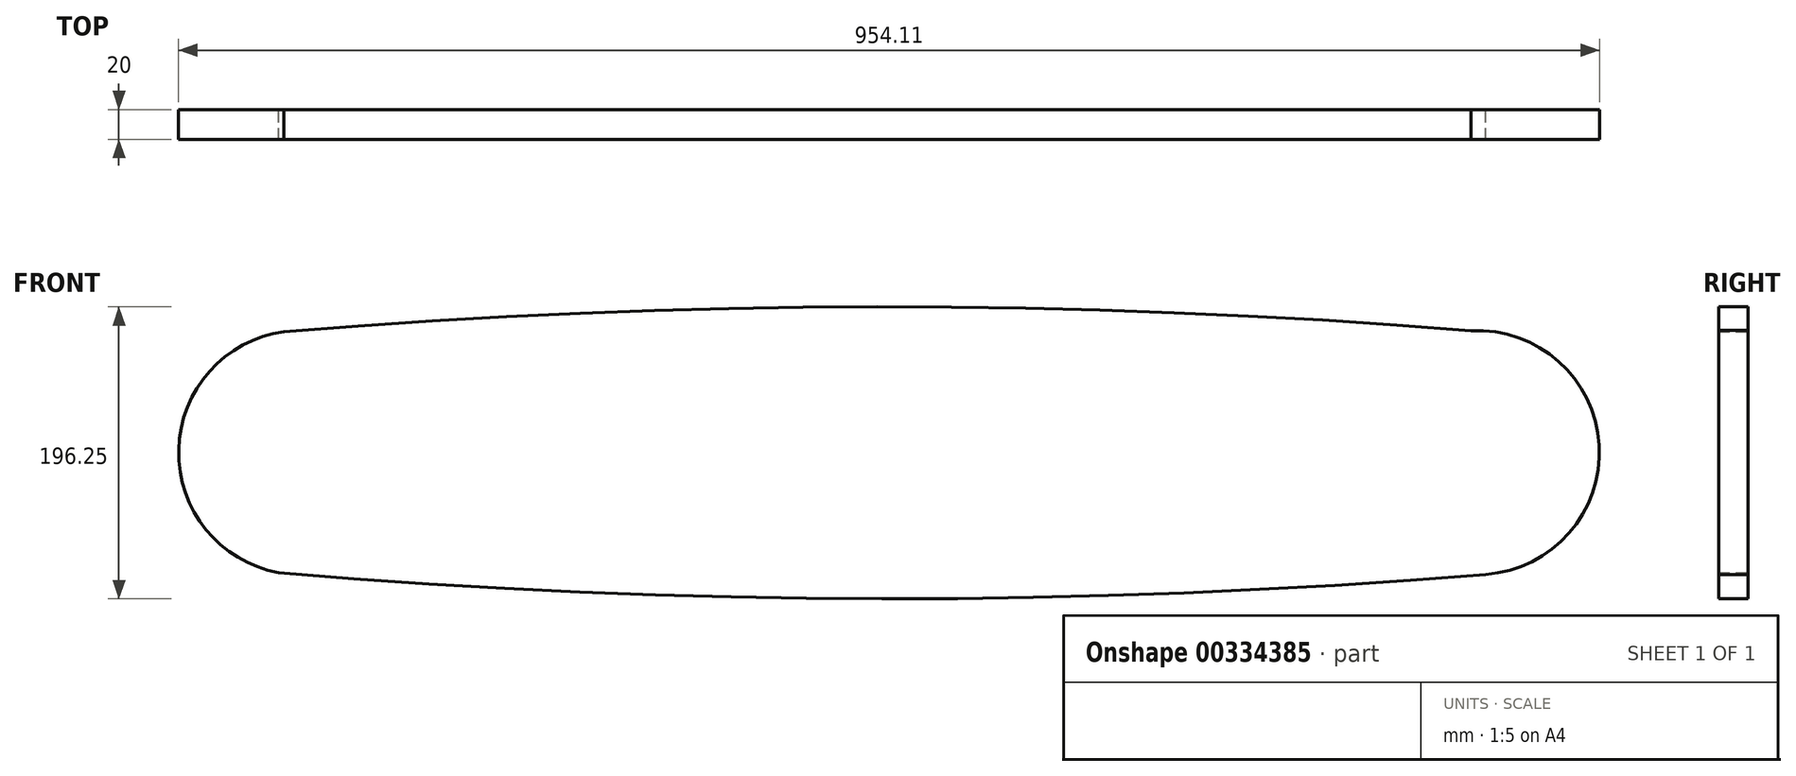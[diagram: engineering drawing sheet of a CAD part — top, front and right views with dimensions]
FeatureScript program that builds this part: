
annotation { "Feature Type Name" : "Feature", "Feature Type Description" : "" }
export const myFeature = defineFeature(function(context is Context, id is Id, definition is map)
    precondition{}
    {
        {
            var Q0;
            Q0=qCreatedBy(makeId("Front.planeOp"),FACE);
            var sketch = newSketch(context, id + "F0", { "sketchPlane" : qUnion([Q0])});
            skCircle(sketch, "E0", {"center": v(-47.6, 0) * mm, "radius": 82.06 * mm});
            skCircle(sketch, "E1", {"center": v(742.4, 0) * mm, "radius": 82.06 * mm});
            skLineSegment(sketch, "E2", {"start": v(-47.6, 0) * mm, "end": v(742.4, 0) * mm});
            skArc(sketch, "E3", {"start": v(-62.59, -80.67) * mm, "mid": v(342.73, -98.23) * mm, "end": v(748.1, -81.86) * mm});
            skArc(sketch, "E4", {"start": v(738.11, 81.94) * mm, "mid": v(339.6, 98) * mm, "end": v(-58.9, 81.27) * mm});
            skSolve(sketch);
        }
        {
            var Q0;
            {var subQ1=sQuery(id+"F0.wireOp",EDGE,"E0");var subQ5=sQuery(id+"F0.wireOp",EDGE,"E4");var subQ7=makeQuery(id+"F0.imprint","INTERSECT",VERTEX,{"disambiguationData":[OD(1.0)],"derivedFrom":[subQ1,subQ5]});Q0=makeQuery(id+"F0.imprint","IMPRINT",FACE,{"disambiguationData":[TD([[makeQuery(id+"F0.imprint","IMPRINT",EDGE,{"disambiguationData":[TD([[subQ7,1.0]])],"derivedFrom":subQ1}),1.0]])]});}
            var Q1;
            {var subQ0=sQuery(id+"F0.wireOp",EDGE,"E4");var subQ1=sQuery(id+"F0.wireOp",EDGE,"E0");var subQ2=makeQuery(id+"F0.imprint","INTERSECT",VERTEX,{"disambiguationData":[OD(1.0)],"derivedFrom":[subQ1,subQ0]});Q1=makeQuery(id+"F0.imprint","IMPRINT",FACE,{"disambiguationData":[TD([[makeQuery(id+"F0.imprint","IMPRINT",EDGE,{"disambiguationData":[TD([[subQ2,1.0]])],"derivedFrom":subQ1}),-1.0]])]});}
            var Q2;
            {var subQ0=sQuery(id+"F0.wireOp",EDGE,"E2");var subQ1=sQuery(id+"F0.wireOp",EDGE,"E0");var subQ2=makeQuery(id+"F0.imprint","INTERSECT",VERTEX,{"derivedFrom":[subQ1,subQ0]});Q2=makeQuery(id+"F0.imprint","IMPRINT",FACE,{"disambiguationData":[TD([[makeQuery(id+"F0.imprint","IMPRINT",EDGE,{"disambiguationData":[TD([[subQ2,1.0]])],"derivedFrom":subQ1}),-1.0]])]});}
            var Q3;
            {var subQ0=sQuery(id+"F0.wireOp",EDGE,"E1");var subQ1=makeQuery(id+"F0.imprint","INTERSECT",VERTEX,{"derivedFrom":[subQ0,sQuery(id+"F0.wireOp",EDGE,"E4")]});Q3=makeQuery(id+"F0.imprint","IMPRINT",FACE,{"disambiguationData":[TD([[makeQuery(id+"F0.imprint","IMPRINT",EDGE,{"disambiguationData":[TD([[subQ1,-1.0]])],"derivedFrom":subQ0}),1.0]])]});}
            extrude(context, id + "F1", {"entities" : qUnion([Q0, Q1, Q2, Q3]), "depth" : 20 * mm});
        }
    });
